# Revit family: Haworth_Openest_ChickPouf
name_source: partatom
category: Furniture
revit_build: Autodesk Revit 2018 (Build: 20170223_1515(x64)
units: mm (PartAtom-declared; Revit-internal decimal feet)

## family parameters
Always vertical = Yes
Cut with Voids When Loaded = No
OmniClass Number = 23.40.20.00
OmniClass Title = General Furniture and Specialties
Room Calculation Point = No
Shared = No
Work Plane-Based = No

## types (3) — shared parameters
Assembly Code = E2020200
Description = Chick Pouf
Manufacturer = Haworth
Model = SOPB
Revision No. = 2
Size = Verify Final Dim. w/ Haworth
Sustainability Info = https://www.haworth.com
URL = http://www.haworth.com
URL - Product = https://www.haworth.com
Warranty = http://www.haworth.com

## per-type parameters (varying)
| type | No Seat Backrest | Seat Backrest | Seat Backrest Down |
| Without Backrest | Yes | No | No |
| With Backrest | No | Yes | No |
| With Seat Backrest Down | No | No | Yes |

## geometry (parser evidence)
native form markers: Sweep x7
no freeform markers — native parametric forms only
